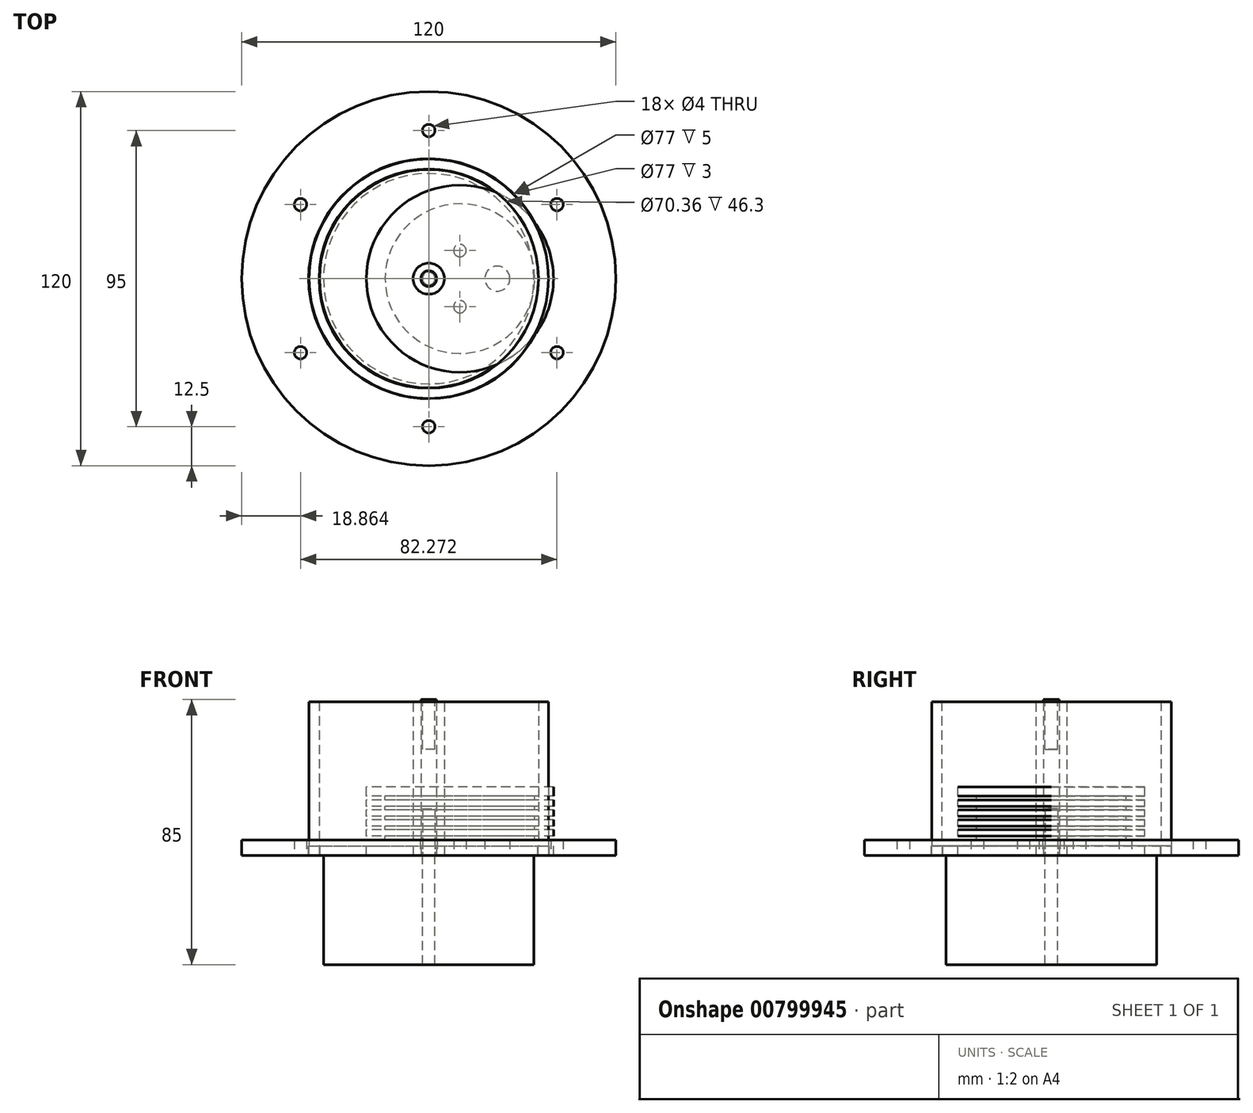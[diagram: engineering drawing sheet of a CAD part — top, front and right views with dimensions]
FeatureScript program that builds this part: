
annotation { "Feature Type Name" : "Feature", "Feature Type Description" : "" }
export const myFeature = defineFeature(function(context is Context, id is Id, definition is map)
    precondition{}
    {
        {
            var Q0;
            Q0=qCreatedBy(makeId("Top.planeOp"),FACE);
            var sketch = newSketch(context, id + "F0", { "sketchPlane" : qUnion([Q0])});
            skCircle(sketch, "E0", {"center": v(0, 0) * mm, "radius": 60 * mm});
            skCircle(sketch, "E1", {"center": v(0, 0) * mm, "radius": 47.5 * mm, "construction": true});
            skLineSegment(sketch, "E2.0", {"start": v(0, 47.5) * mm, "end": v(41.14, 23.75) * mm, "construction": true});
            skLineSegment(sketch, "E2.1", {"start": v(41.14, 23.75) * mm, "end": v(41.14, -23.75) * mm, "construction": true});
            skLineSegment(sketch, "E2.2", {"start": v(41.14, -23.75) * mm, "end": v(0, -47.5) * mm, "construction": true});
            skLineSegment(sketch, "E2.3", {"start": v(0, -47.5) * mm, "end": v(-41.14, -23.75) * mm, "construction": true});
            skLineSegment(sketch, "E2.4", {"start": v(-41.14, -23.75) * mm, "end": v(-41.14, 23.75) * mm, "construction": true});
            skLineSegment(sketch, "E2.5", {"start": v(-41.14, 23.75) * mm, "end": v(0, 47.5) * mm, "construction": true});
            skCircle(sketch, "E3", {"center": v(0, 47.5) * mm, "radius": 2 * mm});
            skCircle(sketch, "E4", {"center": v(41.14, 23.75) * mm, "radius": 2 * mm});
            skCircle(sketch, "E5", {"center": v(41.14, -23.75) * mm, "radius": 2 * mm});
            skCircle(sketch, "E6", {"center": v(0, -47.5) * mm, "radius": 2 * mm});
            skCircle(sketch, "E7", {"center": v(-41.14, -23.75) * mm, "radius": 2 * mm});
            skCircle(sketch, "E8", {"center": v(-41.14, 23.75) * mm, "radius": 2 * mm});
            skSolve(sketch);
        }
        {
            var Q0;
            Q0 = qSketchRegion(id + "F0", true);
            extrude(context, id + "F1", {"entities" : qUnion([Q0]), "depth" : 5 * mm, "offsetDistance" : 25 * mm});
        }
        {
            var Q0;
            Q0=makeQuery(id+"F1.opExtrude","CAP_FACE",FACE,{"disambiguationData":[OSD([sQuery(id+"F0.wireOp",EDGE,"E0"),sQuery(id+"F0.wireOp",EDGE,"E3"),sQuery(id+"F0.wireOp",EDGE,"E4"),sQuery(id+"F0.wireOp",EDGE,"E5"),sQuery(id+"F0.wireOp",EDGE,"E6"),sQuery(id+"F0.wireOp",EDGE,"E7"),sQuery(id+"F0.wireOp",EDGE,"E8")])],"isStart":false});
            var sketch = newSketch(context, id + "F2", { "sketchPlane" : qUnion([Q0])});
            skCircle(sketch, "E9", {"center": v(0, 0) * mm, "radius": 35 * mm});
            skCircle(sketch, "E10", {"center": v(0, 0) * mm, "radius": 38.5 * mm});
            skSolve(sketch);
        }
        {
            var Q0;
            Q0 = qSketchRegion(id + "F2", true);
            extrude(context, id + "F3", {"entities" : qUnion([Q0]), "operationType" : NewBodyOperationType.REMOVE, "oppositeDirection" : true, "depth" : 2.5 * mm, "offsetDistance" : 25 * mm});
        }
        {
            var Q0;
            Q0=qCreatedBy(makeId("Top.planeOp"),FACE);
            var sketch = newSketch(context, id + "F4", { "sketchPlane" : qUnion([Q0])});
            skCircle(sketch, "E11", {"center": v(0, 0) * mm, "radius": 35 * mm});
            skCircle(sketch, "E12", {"center": v(0, 0) * mm, "radius": 38.5 * mm});
            skSolve(sketch);
        }
        {
            var Q0;
            Q0 = qSketchRegion(id + "F4", true);
            extrude(context, id + "F5", {"entities" : qUnion([Q0]), "depth" : 1.5 * mm, "offsetDistance" : 25 * mm});
        }
        {
            var Q0;
            Q0=qCreatedBy(makeId("Top.planeOp"),FACE);
            var sketch = newSketch(context, id + "F6", { "sketchPlane" : qUnion([Q0])});
            skCircle(sketch, "E13", {"center": v(0, 0) * mm, "radius": 35.18 * mm});
            skCircle(sketch, "E14", {"center": v(0, 0) * mm, "radius": 38.4 * mm});
            skSolve(sketch);
        }
        {
            var Q0;
            Q0 = qSketchRegion(id + "F6", true);
            extrude(context, id + "F7", {"entities" : qUnion([Q0]), "depth" : 49.3 * mm, "offsetDistance" : 25 * mm});
        }
        {
            var Q0;
            Q0=qCreatedBy(makeId("Top.planeOp"),FACE);
            var sketch = newSketch(context, id + "F8", { "sketchPlane" : qUnion([Q0])});
            skCircle(sketch, "E15", {"center": v(0, 0) * mm, "radius": 5 * mm});
            skSolve(sketch);
        }
        {
            var Q0;
            Q0 = qSketchRegion(id + "F8", true);
            extrude(context, id + "F9", {"entities" : qUnion([Q0]), "depth" : 49.1 * mm, "offsetDistance" : 25 * mm});
        }
        {
            var Q0;
            Q0=makeQuery(id+"F9.opExtrude","CAP_FACE",FACE,{"disambiguationData":[OSD([sQuery(id+"F8.wireOp",EDGE,"E15")])],"isStart":false});
            var sketch = newSketch(context, id + "F10", { "sketchPlane" : qUnion([Q0])});
            skCircle(sketch, "E16", {"center": v(0, 0) * mm, "radius": 2 * mm});
            skSolve(sketch);
        }
        {
            var Q0;
            Q0 = qSketchRegion(id + "F10", true);
            extrude(context, id + "F11", {"entities" : qUnion([Q0]), "operationType" : NewBodyOperationType.REMOVE, "oppositeDirection" : true, "depth" : 15 * mm, "offsetDistance" : 25 * mm});
        }
        {
            var Q0;
            Q0=makeQuery(id+"F9.opExtrude","CAP_FACE",FACE,{"disambiguationData":[OSD([sQuery(id+"F8.wireOp",EDGE,"E15")])],"isStart":true});
            var sketch = newSketch(context, id + "F12", { "sketchPlane" : qUnion([Q0])});
            skCircle(sketch, "E17", {"center": v(0, 0) * mm, "radius": 2 * mm});
            skSolve(sketch);
        }
        {
            var Q0;
            Q0 = qSketchRegion(id + "F12", true);
            extrude(context, id + "F13", {"entities" : qUnion([Q0]), "operationType" : NewBodyOperationType.REMOVE, "oppositeDirection" : true, "depth" : 15 * mm, "offsetDistance" : 25 * mm});
        }
        {
            var Q0;
            Q0=qCreatedBy(makeId("Top.planeOp"),FACE);
            var sketch = newSketch(context, id + "F14", { "sketchPlane" : qUnion([Q0])});
            skCircle(sketch, "E18", {"center": v(0, 0) * mm, "radius": 33.75 * mm});
            skCircle(sketch, "E19", {"center": v(0, 0) * mm, "radius": 2 * mm});
            skSolve(sketch);
        }
        {
            var Q0;
            Q0 = qSketchRegion(id + "F14", true);
            extrude(context, id + "F15", {"entities" : qUnion([Q0]), "oppositeDirection" : true, "depth" : 35 * mm, "offsetDistance" : 25 * mm});
        }
        {
            var Q0;
            Q0=qCreatedBy(makeId("Top.planeOp"),FACE);
            var sketch = newSketch(context, id + "F16", { "sketchPlane" : qUnion([Q0])});
            skCircle(sketch, "E20", {"center": v(0, 0) * mm, "radius": 60 * mm});
            skCircle(sketch, "E21", {"center": v(0, 0) * mm, "radius": 47.5 * mm, "construction": true});
            skLineSegment(sketch, "E22.0", {"start": v(0, 47.5) * mm, "end": v(41.14, 23.75) * mm, "construction": true});
            skLineSegment(sketch, "E22.1", {"start": v(41.14, 23.75) * mm, "end": v(41.14, -23.75) * mm, "construction": true});
            skLineSegment(sketch, "E22.2", {"start": v(41.14, -23.75) * mm, "end": v(0, -47.5) * mm, "construction": true});
            skLineSegment(sketch, "E22.3", {"start": v(0, -47.5) * mm, "end": v(-41.14, -23.75) * mm, "construction": true});
            skLineSegment(sketch, "E22.4", {"start": v(-41.14, -23.75) * mm, "end": v(-41.14, 23.75) * mm, "construction": true});
            skLineSegment(sketch, "E22.5", {"start": v(-41.14, 23.75) * mm, "end": v(0, 47.5) * mm, "construction": true});
            skCircle(sketch, "E23", {"center": v(0, 47.5) * mm, "radius": 2 * mm});
            skCircle(sketch, "E24", {"center": v(41.14, 23.75) * mm, "radius": 2 * mm});
            skCircle(sketch, "E25", {"center": v(41.14, -23.75) * mm, "radius": 2 * mm});
            skCircle(sketch, "E26", {"center": v(0, -47.5) * mm, "radius": 2 * mm});
            skCircle(sketch, "E27", {"center": v(-41.14, -23.75) * mm, "radius": 2 * mm});
            skCircle(sketch, "E28", {"center": v(-41.14, 23.75) * mm, "radius": 2 * mm});
            skCircle(sketch, "E29", {"center": v(0, 0) * mm, "radius": 2.75 * mm});
            skCircle(sketch, "E30", {"center": v(22, 0) * mm, "radius": 4 * mm});
            skSolve(sketch);
        }
        {
            var Q0;
            Q0 = qSketchRegion(id + "F16", true);
            extrude(context, id + "F17", {"entities" : qUnion([Q0]), "depth" : 5 * mm, "offsetDistance" : 25 * mm});
        }
        {
            var Q0;
            Q0=makeQuery(id+"F17.opExtrude","CAP_FACE",FACE,{"disambiguationData":[OSD([sQuery(id+"F16.wireOp",EDGE,"E20"),sQuery(id+"F16.wireOp",EDGE,"E23"),sQuery(id+"F16.wireOp",EDGE,"E24"),sQuery(id+"F16.wireOp",EDGE,"E25"),sQuery(id+"F16.wireOp",EDGE,"E26"),sQuery(id+"F16.wireOp",EDGE,"E27"),sQuery(id+"F16.wireOp",EDGE,"E28"),sQuery(id+"F16.wireOp",EDGE,"E29"),sQuery(id+"F16.wireOp",EDGE,"E30")])],"isStart":true});
            var sketch = newSketch(context, id + "F18", { "sketchPlane" : qUnion([Q0])});
            skCircle(sketch, "E31", {"center": v(0, 0) * mm, "radius": 35 * mm});
            skCircle(sketch, "E32", {"center": v(0, 0) * mm, "radius": 38.5 * mm});
            skSolve(sketch);
        }
        {
            var Q0;
            Q0 = qSketchRegion(id + "F18", true);
            extrude(context, id + "F19", {"entities" : qUnion([Q0]), "operationType" : NewBodyOperationType.REMOVE, "oppositeDirection" : true, "depth" : 3 * mm, "offsetDistance" : 25 * mm});
        }
        {
            var Q0;
            {var subQ0=sQuery(id+"F16.wireOp",EDGE,"E29");var subQ1=sQuery(id+"F16.wireOp",EDGE,"E30");Q0=makeQuery(id+"F19.boolean.opBoolean","SPLIT",FACE,{"disambiguationData":[TD([makeQuery(id+"F17.opExtrude","SWEPT_FACE",FACE,{"disambiguationData":[OSD([subQ0])]})])],"derivedFrom":makeQuery(id+"F17.opExtrude","CAP_FACE",FACE,{"disambiguationData":[OSD([sQuery(id+"F16.wireOp",EDGE,"E20"),sQuery(id+"F16.wireOp",EDGE,"E23"),sQuery(id+"F16.wireOp",EDGE,"E24"),sQuery(id+"F16.wireOp",EDGE,"E25"),sQuery(id+"F16.wireOp",EDGE,"E26"),sQuery(id+"F16.wireOp",EDGE,"E27"),sQuery(id+"F16.wireOp",EDGE,"E28"),subQ0,subQ1])],"isStart":true})});}
            var sketch = newSketch(context, id + "F20", { "sketchPlane" : qUnion([Q0])});
            skCircle(sketch, "E33", {"center": v(10, 9) * mm, "radius": 2 * mm});
            skCircle(sketch, "E34", {"center": v(10, -9) * mm, "radius": 2 * mm});
            skSolve(sketch);
        }
        {
            var Q0;
            Q0 = qSketchRegion(id + "F20", true);
            extrude(context, id + "F21", {"entities" : qUnion([Q0]), "operationType" : NewBodyOperationType.REMOVE, "endBound" : BoundingType.THROUGH_ALL, "oppositeDirection" : true, "depth" : 5 * mm, "offsetDistance" : 25 * mm});
        }
        {
            var Q0;
            Q0=qCreatedBy(makeId("Front.planeOp"),FACE);
            var sketch = newSketch(context, id + "F22", { "sketchPlane" : qUnion([Q0])});
            skLineSegment(sketch, "E35", {"start": v(10, 0) * mm, "end": v(40, 0) * mm});
            skLineSegment(sketch, "E36", {"start": v(40, 0) * mm, "end": v(40, 5) * mm});
            skLineSegment(sketch, "E37", {"start": v(40, 5) * mm, "end": v(34, 5) * mm});
            skLineSegment(sketch, "E38", {"start": v(34, 5) * mm, "end": v(34, 6.2) * mm});
            skLineSegment(sketch, "E39", {"start": v(34, 6.2) * mm, "end": v(40, 6.2) * mm});
            skLineSegment(sketch, "E40", {"start": v(40, 6.2) * mm, "end": v(40, 8.2) * mm});
            skLineSegment(sketch, "E41", {"start": v(40, 8.2) * mm, "end": v(34, 8.2) * mm});
            skLineSegment(sketch, "E42", {"start": v(34, 8.2) * mm, "end": v(34, 9.4) * mm});
            skLineSegment(sketch, "E43", {"start": v(34, 9.4) * mm, "end": v(40, 9.4) * mm});
            skLineSegment(sketch, "E44", {"start": v(40, 9.4) * mm, "end": v(40, 11.4) * mm});
            skLineSegment(sketch, "E45", {"start": v(40, 11.4) * mm, "end": v(34, 11.4) * mm});
            skLineSegment(sketch, "E46", {"start": v(34, 11.4) * mm, "end": v(34, 12.6) * mm});
            skLineSegment(sketch, "E47", {"start": v(34, 12.6) * mm, "end": v(40, 12.6) * mm});
            skLineSegment(sketch, "E48", {"start": v(40, 12.6) * mm, "end": v(40, 14.6) * mm});
            skLineSegment(sketch, "E49", {"start": v(40, 14.6) * mm, "end": v(34, 14.6) * mm});
            skLineSegment(sketch, "E50", {"start": v(34, 14.6) * mm, "end": v(34, 15.8) * mm});
            skLineSegment(sketch, "E51", {"start": v(34, 15.8) * mm, "end": v(40, 15.8) * mm});
            skLineSegment(sketch, "E52", {"start": v(40, 15.8) * mm, "end": v(40, 17.8) * mm});
            skLineSegment(sketch, "E53", {"start": v(40, 17.8) * mm, "end": v(34, 17.8) * mm});
            skLineSegment(sketch, "E54", {"start": v(34, 17.8) * mm, "end": v(34, 19) * mm});
            skLineSegment(sketch, "E55", {"start": v(34, 19) * mm, "end": v(40, 19) * mm});
            skLineSegment(sketch, "E56", {"start": v(40, 19) * mm, "end": v(40, 22) * mm});
            skLineSegment(sketch, "E57", {"start": v(40, 22) * mm, "end": v(10, 22) * mm});
            skLineSegment(sketch, "E58", {"start": v(10, 22) * mm, "end": v(10, 0) * mm});
            skSolve(sketch);
        }
        {
            var Q0;
            Q0 = qSketchRegion(id + "F22", true);
            var Q1;
            Q1=sQuery(id+"F22.wireOp",EDGE,"E58");
            revolve(context, id + "F23", {"surfaceOperationType" : NewSurfaceOperationType.NEW, "entities" : qUnion([Q0]), "axis" : qUnion([Q1]), "revolveType" : RevolveType.FULL});
        }
        {
            var Q0;
            Q0=qCreatedBy(makeId("Top.planeOp"),FACE);
            var sketch = newSketch(context, id + "F24", { "sketchPlane" : qUnion([Q0])});
            skCircle(sketch, "E59", {"center": v(0, 0) * mm, "radius": 2.5 * mm});
            skSolve(sketch);
        }
        {
            var Q0;
            Q0 = qSketchRegion(id + "F24", true);
            extrude(context, id + "F25", {"entities" : qUnion([Q0]), "depth" : 50 * mm, "offsetDistance" : 25 * mm});
        }
    });
